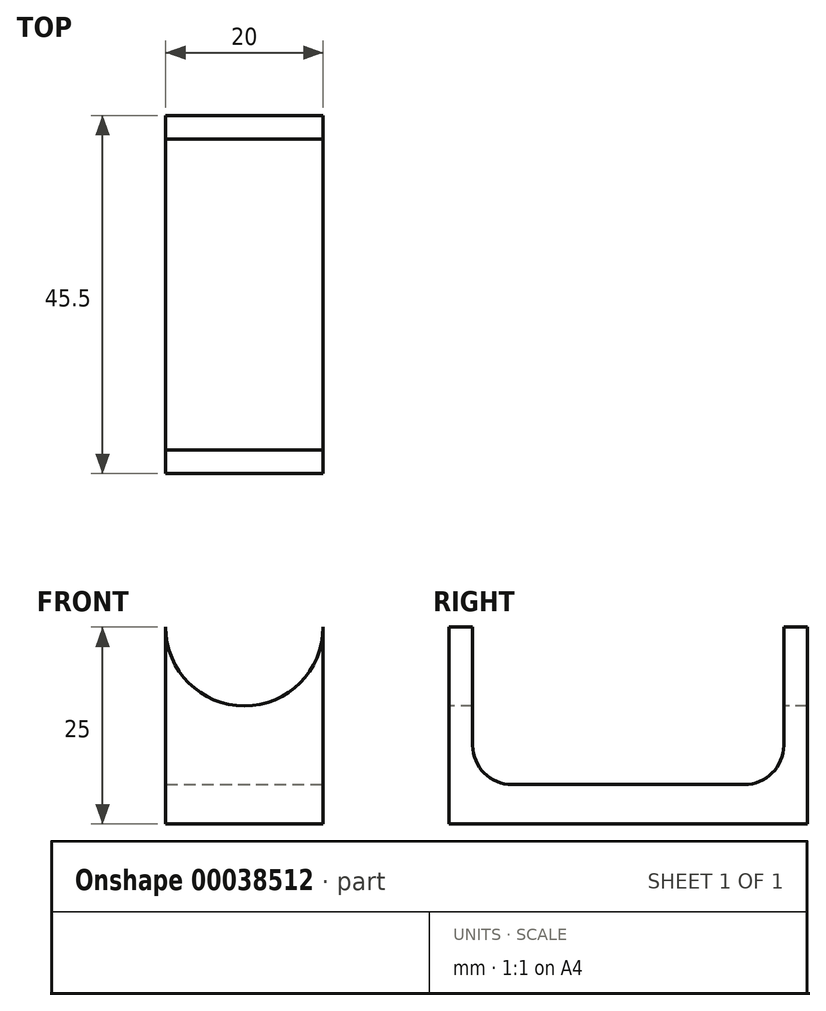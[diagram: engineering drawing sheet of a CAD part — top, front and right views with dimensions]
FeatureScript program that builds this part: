
annotation { "Feature Type Name" : "Feature", "Feature Type Description" : "" }
export const myFeature = defineFeature(function(context is Context, id is Id, definition is map)
    precondition{}
    {
        {
            var Q0;
            Q0=qCreatedBy(makeId("Front.planeOp"),FACE);
            var sketch = newSketch(context, id + "F0", { "sketchPlane" : qUnion([Q0])});
            skCircle(sketch, "E0", {"center": v(0, 0) * mm, "radius": 10 * mm});
            skCircle(sketch, "E1", {"center": v(0, 0) * mm, "radius": 5 * mm});
            skCircle(sketch, "E2", {"center": v(0, 0) * mm, "radius": 7 * mm, "construction": true});
            skPoint(sketch, "E3", {"position": v(4.95, -4.95) * mm});
            skLineSegment(sketch, "E4", {"start": v(0, 0) * mm, "end": v(0, -7) * mm, "construction": true});
            skLineSegment(sketch, "E5", {"start": v(0, 0) * mm, "end": v(7, 0) * mm, "construction": true});
            skCircle(sketch, "E6", {"center": v(0, -7) * mm, "radius": 0.8 * mm});
            skCircle(sketch, "E7", {"center": v(4.95, -4.95) * mm, "radius": 0.8 * mm});
            skCircle(sketch, "E8", {"center": v(7, 0) * mm, "radius": 0.8 * mm});
            skCircle(sketch, "E9.MirrorC", {"center": v(-4.95, -4.95) * mm, "radius": 0.8 * mm});
            skCircle(sketch, "E10.MirrorC", {"center": v(-7, 0) * mm, "radius": 0.8 * mm});
            skCircle(sketch, "E11.MirrorC", {"center": v(0, 7) * mm, "radius": 0.8 * mm});
            skLineSegment(sketch, "E12", {"start": v(0, 0) * mm, "end": v(0, -25) * mm, "construction": true});
            skLineSegment(sketch, "E13", {"start": v(0, -25) * mm, "end": v(-10, -25) * mm});
            skLineSegment(sketch, "E14.MirrorCS", {"start": v(0, -25) * mm, "end": v(10, -25) * mm});
            skLineSegment(sketch, "E15", {"start": v(-10, -25) * mm, "end": v(-10, 0) * mm});
            skLineSegment(sketch, "E16.MirrorCS", {"start": v(10, -25) * mm, "end": v(10, 0) * mm});
            skLineSegment(sketch, "E17", {"start": v(-10, 0) * mm, "end": v(10, 0) * mm, "construction": true});
            skLineSegment(sketch, "E18", {"start": v(-10, -22) * mm, "end": v(10, -22) * mm});
            skLineSegment(sketch, "E19", {"start": v(-10, 0) * mm, "end": v(-10, 10) * mm});
            skLineSegment(sketch, "E20", {"start": v(-10, 10) * mm, "end": v(10, 10) * mm});
            skLineSegment(sketch, "E21", {"start": v(10, 10) * mm, "end": v(10, 0) * mm});
            skSolve(sketch);
        }
        {
            var Q0;
            {var subQ4=sQuery(id+"F0.wireOp",EDGE,"E13");Q0=makeQuery(id+"F0.imprint","IMPRINT",FACE,{"disambiguationData":[TD([[makeQuery(id+"F0.imprint","IMPRINT",EDGE,{"derivedFrom":subQ4}),-1.0]])]});}
            var Q1;
            {var subQ0=sQuery(id+"F0.wireOp",EDGE,"E21");Q1=makeQuery(id+"F0.imprint","IMPRINT",FACE,{"disambiguationData":[TD([[makeQuery(id+"F0.imprint","IMPRINT",EDGE,{"derivedFrom":subQ0}),-1.0]])]});}
            var Q2;
            {var subQ0=sQuery(id+"F0.wireOp",EDGE,"E19");Q2=makeQuery(id+"F0.imprint","IMPRINT",FACE,{"disambiguationData":[TD([[makeQuery(id+"F0.imprint","IMPRINT",EDGE,{"derivedFrom":subQ0}),-1.0]])]});}
            var Q3;
            Q3=makeQuery(id+"F0.imprint","IMPRINT",FACE,{"disambiguationData":[TD([[makeQuery(id+"F0.imprint","IMPRINT",EDGE,{"derivedFrom":sQuery(id+"F0.wireOp",EDGE,"E1")}),1.0]])]});
            var Q4;
            Q4=makeQuery(id+"F0.imprint","IMPRINT",FACE,{"disambiguationData":[TD([[makeQuery(id+"F0.imprint","IMPRINT",EDGE,{"derivedFrom":sQuery(id+"F0.wireOp",EDGE,"E6")}),1.0]])]});
            var Q5;
            Q5=makeQuery(id+"F0.imprint","IMPRINT",FACE,{"disambiguationData":[TD([[makeQuery(id+"F0.imprint","IMPRINT",EDGE,{"derivedFrom":sQuery(id+"F0.wireOp",EDGE,"E8")}),1.0]])]});
            var Q6;
            Q6=makeQuery(id+"F0.imprint","IMPRINT",FACE,{"disambiguationData":[TD([[makeQuery(id+"F0.imprint","IMPRINT",EDGE,{"derivedFrom":sQuery(id+"F0.wireOp",EDGE,"E9.MirrorC")}),-1.0]])]});
            var Q7;
            Q7=makeQuery(id+"F0.imprint","IMPRINT",FACE,{"disambiguationData":[TD([[makeQuery(id+"F0.imprint","IMPRINT",EDGE,{"derivedFrom":sQuery(id+"F0.wireOp",EDGE,"E10.MirrorC")}),-1.0]])]});
            var Q8;
            Q8=makeQuery(id+"F0.imprint","IMPRINT",FACE,{"disambiguationData":[TD([[makeQuery(id+"F0.imprint","IMPRINT",EDGE,{"derivedFrom":sQuery(id+"F0.wireOp",EDGE,"E11.MirrorC")}),-1.0]])]});
            var Q9;
            {var subQ5=sQuery(id+"F0.wireOp",EDGE,"E18");Q9=makeQuery(id+"F0.imprint","IMPRINT",FACE,{"disambiguationData":[TD([[makeQuery(id+"F0.imprint","IMPRINT",EDGE,{"derivedFrom":subQ5}),1.0]])]});}
            var Q10;
            Q10=makeQuery(id+"F0.imprint","IMPRINT",FACE,{"disambiguationData":[TD([[makeQuery(id+"F0.imprint","IMPRINT",EDGE,{"derivedFrom":sQuery(id+"F0.wireOp",EDGE,"E1")}),-1.0]])]});
            var Q11;
            Q11=makeQuery(id+"F0.imprint","IMPRINT",FACE,{"disambiguationData":[TD([[makeQuery(id+"F0.imprint","IMPRINT",EDGE,{"derivedFrom":sQuery(id+"F0.wireOp",EDGE,"E7")}),1.0]])]});
            extrude(context, id + "F1", {"entities" : qUnion([Q0, Q1, Q2, Q3, Q4, Q5, Q6, Q7, Q8, Q9, Q10, Q11]), "oppositeDirection" : true, "depth" : 45.5 * mm, "offsetDistance" : 25 * mm});
        }
        {
            var Q0;
            Q0=makeQuery(id+"F1.opExtrude","SWEPT_FACE",FACE,{"disambiguationData":[OSD([sQuery(id+"F0.wireOp",EDGE,"E16.MirrorCS"),sQuery(id+"F0.wireOp",EDGE,"E21")])]});
            var sketch = newSketch(context, id + "F2", { "sketchPlane" : qUnion([Q0])});
            skLineSegment(sketch, "E22", {"start": v(3, 10) * mm, "end": v(3, -20) * mm});
            skLineSegment(sketch, "E23", {"start": v(3, -20) * mm, "end": v(42.5, -20) * mm});
            skLineSegment(sketch, "E24", {"start": v(42.5, -20) * mm, "end": v(42.5, 10) * mm});
            skSolve(sketch);
        }
        {
            var Q0;
            {var subQ0=sQuery(id+"F2.wireOp",EDGE,"E22");Q0=makeQuery(id+"F2.imprint","IMPRINT",FACE,{"disambiguationData":[TD([[makeQuery(id+"F2.imprint","IMPRINT",EDGE,{"derivedFrom":subQ0}),1.0]])]});}
            extrude(context, id + "F3", {"entities" : qUnion([Q0]), "operationType" : NewBodyOperationType.REMOVE, "endBound" : BoundingType.THROUGH_ALL, "oppositeDirection" : true, "depth" : 25 * mm, "offsetDistance" : 25 * mm});
        }
        {
            var Q0;
            Q0=makeQuery(id+"F0.imprint","IMPRINT",FACE,{"disambiguationData":[TD([[makeQuery(id+"F0.imprint","IMPRINT",EDGE,{"derivedFrom":sQuery(id+"F0.wireOp",EDGE,"E1")}),1.0]])]});
            var Q1;
            {var subQ0=sQuery(id+"F0.wireOp",EDGE,"E19");Q1=makeQuery(id+"F0.imprint","IMPRINT",FACE,{"disambiguationData":[TD([[makeQuery(id+"F0.imprint","IMPRINT",EDGE,{"derivedFrom":subQ0}),-1.0]])]});}
            var Q2;
            {var subQ0=sQuery(id+"F0.wireOp",EDGE,"E21");Q2=makeQuery(id+"F0.imprint","IMPRINT",FACE,{"disambiguationData":[TD([[makeQuery(id+"F0.imprint","IMPRINT",EDGE,{"derivedFrom":subQ0}),-1.0]])]});}
            var Q3;
            Q3=makeQuery(id+"F0.imprint","IMPRINT",FACE,{"disambiguationData":[TD([[makeQuery(id+"F0.imprint","IMPRINT",EDGE,{"derivedFrom":sQuery(id+"F0.wireOp",EDGE,"E8")}),1.0]])]});
            var Q4;
            Q4=makeQuery(id+"F0.imprint","IMPRINT",FACE,{"disambiguationData":[TD([[makeQuery(id+"F0.imprint","IMPRINT",EDGE,{"derivedFrom":sQuery(id+"F0.wireOp",EDGE,"E11.MirrorC")}),-1.0]])]});
            var Q5;
            Q5=makeQuery(id+"F0.imprint","IMPRINT",FACE,{"disambiguationData":[TD([[makeQuery(id+"F0.imprint","IMPRINT",EDGE,{"derivedFrom":sQuery(id+"F0.wireOp",EDGE,"E10.MirrorC")}),-1.0]])]});
            var Q6;
            Q6=makeQuery(id+"F0.imprint","IMPRINT",FACE,{"disambiguationData":[TD([[makeQuery(id+"F0.imprint","IMPRINT",EDGE,{"derivedFrom":sQuery(id+"F0.wireOp",EDGE,"E9.MirrorC")}),-1.0]])]});
            var Q7;
            Q7=makeQuery(id+"F0.imprint","IMPRINT",FACE,{"disambiguationData":[TD([[makeQuery(id+"F0.imprint","IMPRINT",EDGE,{"derivedFrom":sQuery(id+"F0.wireOp",EDGE,"E6")}),1.0]])]});
            var Q8;
            Q8=makeQuery(id+"F0.imprint","IMPRINT",FACE,{"disambiguationData":[TD([[makeQuery(id+"F0.imprint","IMPRINT",EDGE,{"derivedFrom":sQuery(id+"F0.wireOp",EDGE,"E7")}),1.0]])]});
            extrude(context, id + "F4", {"entities" : qUnion([Q0, Q1, Q2, Q3, Q4, Q5, Q6, Q7, Q8]), "operationType" : NewBodyOperationType.REMOVE, "endBound" : BoundingType.THROUGH_ALL, "oppositeDirection" : true, "depth" : 25 * mm, "offsetDistance" : 25 * mm});
        }
        {
            var Q0;
            Q0=makeQuery(id+"FmsPlMjCBMf9qQ8_1.opExtrude","CAP_EDGE",EDGE,{"disambiguationData":[OSD([sQuery(id+"FeUEZ1SVA0MmRYH_1.wireOp",EDGE,"Zp2ejaDW-NZ0c-reCR-q1Yj-4rO3aFS4NyxH")])],"isStart":false});
            var Q1;
            Q1=makeQuery(id+"FmsPlMjCBMf9qQ8_1.opExtrude","CAP_EDGE",EDGE,{"disambiguationData":[OSD([sQuery(id+"FeUEZ1SVA0MmRYH_1.wireOp",EDGE,"f86aaa88-c32a-49d5-87d1-07e0a0bf5b430.MirrorCS")])],"isStart":false});
            var Q2;
            Q2=makeQuery(id+"F3.boolean.opBoolean","COPY",EDGE,{"derivedFrom":makeQuery(id+"F3.opExtrude","SWEPT_EDGE",EDGE,{"disambiguationData":[OSD([sQuery(id+"F2.wireOp",EDGE,"E23"),sQuery(id+"F2.wireOp",EDGE,"E24")])]})});
            var Q3;
            Q3=makeQuery(id+"F3.boolean.opBoolean","COPY",EDGE,{"derivedFrom":makeQuery(id+"F3.opExtrude","SWEPT_EDGE",EDGE,{"disambiguationData":[OSD([sQuery(id+"F2.wireOp",EDGE,"E22"),sQuery(id+"F2.wireOp",EDGE,"E23")])]})});
            fillet(context, id + "F5", {"entities" : qUnion([Q0, Q1, Q2, Q3]), "radius" : 5 * mm, "tangentPropagation" : true, "allowEdgeOverflow" : false});
        }
    });
